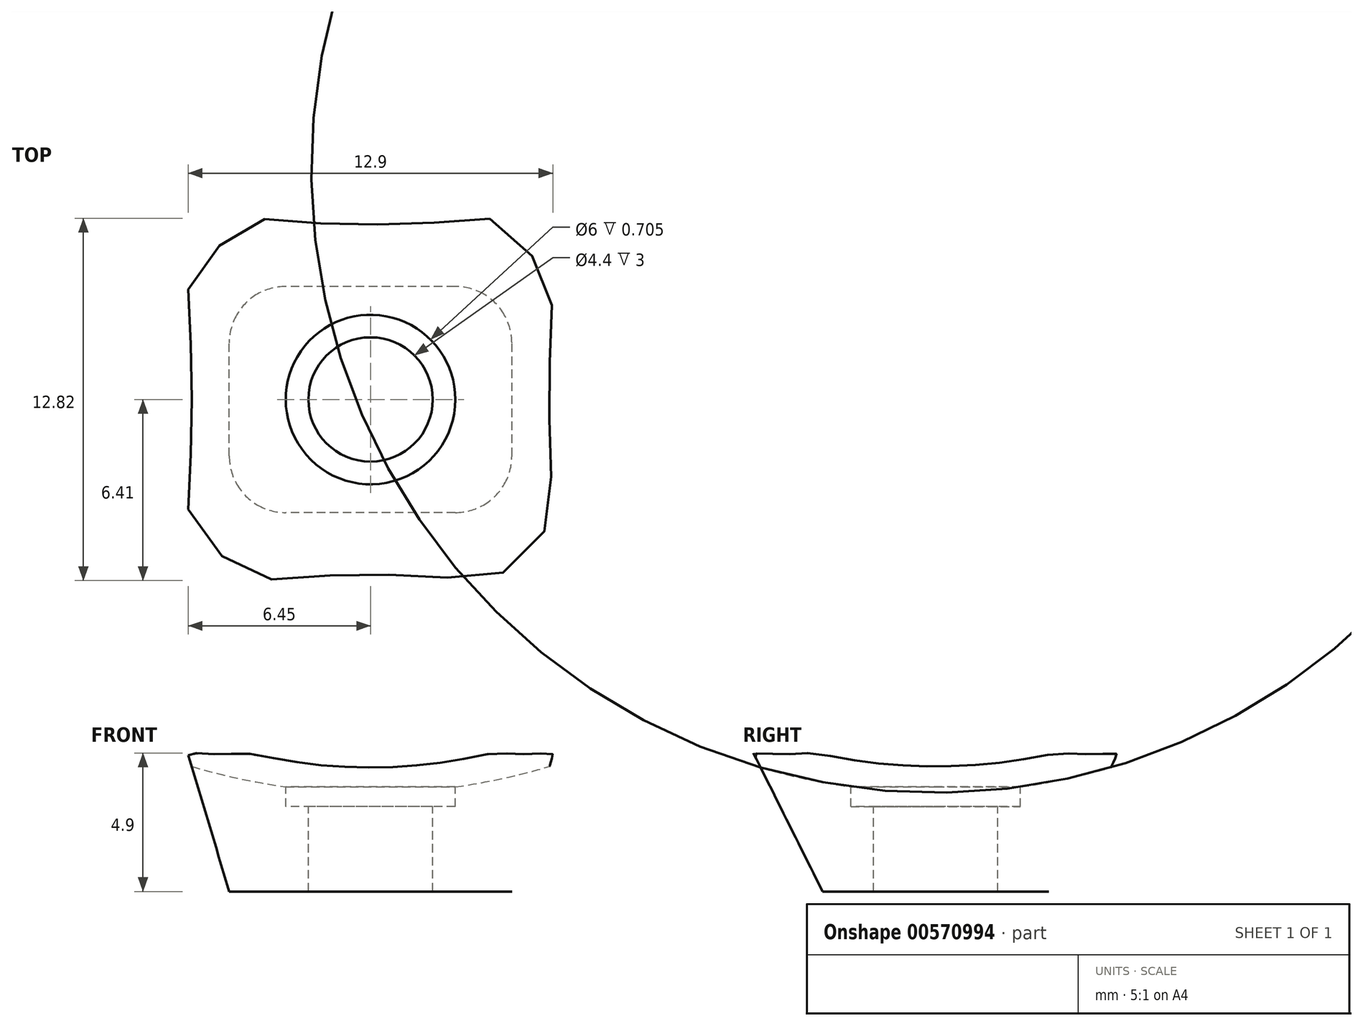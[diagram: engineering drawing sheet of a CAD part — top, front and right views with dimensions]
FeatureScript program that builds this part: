
annotation { "Feature Type Name" : "Feature", "Feature Type Description" : "" }
export const myFeature = defineFeature(function(context is Context, id is Id, definition is map)
    precondition{}
    {
        {
            var Q0;
            Q0=qCreatedBy(makeId("Top.planeOp"),FACE);
            var sketch = newSketch(context, id + "F0", { "sketchPlane" : qUnion([Q0])});
            skLineSegment(sketch, "E0.bottom", {"start": v(3, -4) * mm, "end": v(-3, -4) * mm});
            skLineSegment(sketch, "E0.top", {"start": v(3, 4) * mm, "end": v(-3, 4) * mm});
            skLineSegment(sketch, "E0.left", {"start": v(5, -2) * mm, "end": v(5, 2) * mm});
            skLineSegment(sketch, "E0.right", {"start": v(-5, -2) * mm, "end": v(-5, 2) * mm});
            skPoint(sketch, "E0.middle", {"position": v(0, 0) * mm});
            skPoint(sketch, "E1.visualSharp", {"position": v(-5, 4) * mm});
            skArc(sketch, "E1.filletArc", {"start": v(-3, 4) * mm, "mid": v(-4.41, 3.41) * mm, "end": v(-5, 2) * mm});
            skPoint(sketch, "E2.visualSharp", {"position": v(-5, -4) * mm});
            skArc(sketch, "E2.filletArc", {"start": v(-5, -2) * mm, "mid": v(-4.41, -3.41) * mm, "end": v(-3, -4) * mm});
            skPoint(sketch, "E3.visualSharp", {"position": v(5, -4) * mm});
            skArc(sketch, "E3.filletArc", {"start": v(3, -4) * mm, "mid": v(4.41, -3.41) * mm, "end": v(5, -2) * mm});
            skPoint(sketch, "E4.visualSharp", {"position": v(5, 4) * mm});
            skArc(sketch, "E4.filletArc", {"start": v(5, 2) * mm, "mid": v(4.41, 3.41) * mm, "end": v(3, 4) * mm});
            skSolve(sketch);
        }
        {
            var Q0;
            Q0=qCreatedBy(makeId("Right.planeOp"),FACE);
            var sketch = newSketch(context, id + "F1", { "sketchPlane" : qUnion([Q0])});
            skLineSegment(sketch, "E5", {"start": v(0, 0) * mm, "end": v(0, 5) * mm});
            skLineSegment(sketch, "E6", {"start": v(0, 5) * mm, "end": v(-8, 5) * mm, "construction": true});
            skPoint(sketch, "E7", {"position": v(0, 3.5) * mm});
            skLineSegment(sketch, "E8", {"start": v(0, 3.5) * mm, "end": v(-8, 3.5) * mm, "construction": true});
            skArc(sketch, "E9", {"start": v(-8, 5) * mm, "mid": v(-4.07, 3.88) * mm, "end": v(0, 3.5) * mm});
            skLineSegment(sketch, "E10", {"start": v(0, 5) * mm, "end": v(0, 7.01) * mm});
            skLineSegment(sketch, "E11", {"start": v(0, 7.01) * mm, "end": v(-8, 7.01) * mm});
            skLineSegment(sketch, "E12", {"start": v(-8, 7.01) * mm, "end": v(-8, 5) * mm});
            skLineSegment(sketch, "E13", {"start": v(0, 0) * mm, "end": v(-2.2, 0) * mm});
            skLineSegment(sketch, "E14", {"start": v(-3, 3) * mm, "end": v(-3, 3.7) * mm});
            skLineSegment(sketch, "E15", {"start": v(-2.2, 0) * mm, "end": v(-2.2, 3) * mm});
            skLineSegment(sketch, "E16", {"start": v(-2.2, 3) * mm, "end": v(-3, 3) * mm});
            skSolve(sketch);
        }
        {
            var Q0;
            Q0=qCreatedBy(makeId("Top.planeOp"),FACE);
            var Q1;
            Q1=sQuery(id+"F1.wireOp",VERTEX,"E5.end");
            cPlane(context, id + "F2", {"entities" : qUnion([Q0, Q1]), "cplaneType" : CPlaneType.PLANE_POINT, "offset" : 25 * mm, "width" : 150 * mm, "height" : 150 * mm});
        }
        {
            var Q0;
            Q0=qCreatedBy(id+"F2.planeOp",FACE);
            var sketch = newSketch(context, id + "F3", { "sketchPlane" : qUnion([Q0])});
            skLineSegment(sketch, "E17", {"start": v(-6.5, 3.96) * mm, "end": v(-6.5, -3.96) * mm});
            skLineSegment(sketch, "E18", {"start": v(6.5, 3.96) * mm, "end": v(6.5, -3.96) * mm});
            skLineSegment(sketch, "E19", {"start": v(-3.96, 6.5) * mm, "end": v(3.96, 6.5) * mm});
            skLineSegment(sketch, "E20", {"start": v(-3.96, -6.5) * mm, "end": v(3.96, -6.5) * mm});
            skLineSegment(sketch, "E21", {"start": v(-4.67, 6.2) * mm, "end": v(-6.2, 4.67) * mm});
            skLineSegment(sketch, "E22", {"start": v(4.67, 6.2) * mm, "end": v(6.2, 4.67) * mm});
            skLineSegment(sketch, "E23", {"start": v(6.2, -4.67) * mm, "end": v(4.67, -6.2) * mm});
            skLineSegment(sketch, "E24", {"start": v(-6.2, -4.67) * mm, "end": v(-4.67, -6.2) * mm});
            skPoint(sketch, "E25.visualSharp", {"position": v(-4.38, 6.5) * mm});
            skArc(sketch, "E25.filletArc", {"start": v(-3.96, 6.5) * mm, "mid": v(-4.35, 6.42) * mm, "end": v(-4.67, 6.2) * mm});
            skPoint(sketch, "E26.visualSharp", {"position": v(-6.5, 4.38) * mm});
            skArc(sketch, "E26.filletArc", {"start": v(-6.2, 4.67) * mm, "mid": v(-6.42, 4.35) * mm, "end": v(-6.5, 3.96) * mm});
            skPoint(sketch, "E27.visualSharp", {"position": v(-6.5, -4.38) * mm});
            skArc(sketch, "E27.filletArc", {"start": v(-6.5, -3.96) * mm, "mid": v(-6.42, -4.35) * mm, "end": v(-6.2, -4.67) * mm});
            skPoint(sketch, "E28.visualSharp", {"position": v(-4.38, -6.5) * mm});
            skArc(sketch, "E28.filletArc", {"start": v(-4.67, -6.2) * mm, "mid": v(-4.35, -6.42) * mm, "end": v(-3.96, -6.5) * mm});
            skPoint(sketch, "E29.visualSharp", {"position": v(4.38, -6.5) * mm});
            skArc(sketch, "E29.filletArc", {"start": v(3.96, -6.5) * mm, "mid": v(4.35, -6.42) * mm, "end": v(4.67, -6.2) * mm});
            skPoint(sketch, "E30.visualSharp", {"position": v(6.5, -4.38) * mm});
            skArc(sketch, "E30.filletArc", {"start": v(6.2, -4.67) * mm, "mid": v(6.42, -4.35) * mm, "end": v(6.5, -3.96) * mm});
            skPoint(sketch, "E31.visualSharp", {"position": v(6.5, 4.38) * mm});
            skArc(sketch, "E31.filletArc", {"start": v(6.5, 3.96) * mm, "mid": v(6.42, 4.35) * mm, "end": v(6.2, 4.67) * mm});
            skPoint(sketch, "E32.visualSharp", {"position": v(4.38, 6.5) * mm});
            skArc(sketch, "E32.filletArc", {"start": v(4.67, 6.2) * mm, "mid": v(4.35, 6.42) * mm, "end": v(3.96, 6.5) * mm});
            skSolve(sketch);
        }
        {
            var Q0;
            Q0=sQuery(id+"F3.wireOp",VERTEX,"E30.filletArc.end");
            var Q1;
            Q1=sQuery(id+"F0.wireOp",VERTEX,"E0.left.start");
            var Q2;
            Q2=sQuery(id+"F0.wireOp",VERTEX,"E0.middle");
            cPlane(context, id + "F4", {"entities" : qUnion([Q0, Q1, Q2]), "cplaneType" : CPlaneType.THREE_POINT, "offset" : 25 * mm, "width" : 150 * mm, "height" : 150 * mm});
        }
        {
            var Q0;
            Q0=sQuery(id+"F0.wireOp",VERTEX,"E0.middle");
            var Q1;
            Q1=sQuery(id+"F3.wireOp",VERTEX,"E31.filletArc.start");
            var Q2;
            Q2=sQuery(id+"F0.wireOp",VERTEX,"E0.left.end");
            cPlane(context, id + "F5", {"entities" : qUnion([Q0, Q1, Q2]), "cplaneType" : CPlaneType.THREE_POINT, "offset" : 25 * mm, "width" : 150 * mm, "height" : 150 * mm});
        }
        {
            var Q0;
            Q0=sQuery(id+"F3.wireOp",VERTEX,"E32.filletArc.end");
            var Q1;
            Q1=sQuery(id+"F0.wireOp",VERTEX,"E0.top.start");
            var Q2;
            Q2=sQuery(id+"F0.wireOp",VERTEX,"E0.middle");
            cPlane(context, id + "F6", {"entities" : qUnion([Q0, Q1, Q2]), "cplaneType" : CPlaneType.THREE_POINT, "offset" : 25 * mm, "width" : 150 * mm, "height" : 150 * mm});
        }
        {
            var Q0;
            Q0=sQuery(id+"F0.wireOp",VERTEX,"E0.middle");
            var Q1;
            Q1=sQuery(id+"F3.wireOp",VERTEX,"E25.filletArc.start");
            var Q2;
            Q2=sQuery(id+"F0.wireOp",VERTEX,"E1.filletArc.start");
            cPlane(context, id + "F7", {"entities" : qUnion([Q0, Q1, Q2]), "cplaneType" : CPlaneType.THREE_POINT, "offset" : 25 * mm, "width" : 150 * mm, "height" : 150 * mm});
        }
        {
            var Q0;
            Q0=sQuery(id+"F3.wireOp",VERTEX,"E17.start");
            var Q1;
            Q1=sQuery(id+"F0.wireOp",VERTEX,"E1.filletArc.end");
            var Q2;
            Q2=sQuery(id+"F0.wireOp",VERTEX,"E0.middle");
            cPlane(context, id + "F8", {"entities" : qUnion([Q0, Q1, Q2]), "cplaneType" : CPlaneType.THREE_POINT, "offset" : 25 * mm, "width" : 150 * mm, "height" : 150 * mm});
        }
        {
            var Q0;
            Q0=sQuery(id+"F3.wireOp",VERTEX,"E27.filletArc.start");
            var Q1;
            Q1=sQuery(id+"F0.wireOp",VERTEX,"E2.filletArc.start");
            var Q2;
            Q2=sQuery(id+"F0.wireOp",VERTEX,"E0.middle");
            cPlane(context, id + "F9", {"entities" : qUnion([Q0, Q1, Q2]), "cplaneType" : CPlaneType.THREE_POINT, "offset" : 25 * mm, "width" : 150 * mm, "height" : 150 * mm});
        }
        {
            var Q0;
            Q0=sQuery(id+"F3.wireOp",VERTEX,"E28.filletArc.end");
            var Q1;
            Q1=sQuery(id+"F0.wireOp",VERTEX,"E0.bottom.end");
            var Q2;
            Q2=sQuery(id+"F0.wireOp",VERTEX,"E0.middle");
            cPlane(context, id + "F10", {"entities" : qUnion([Q0, Q1, Q2]), "cplaneType" : CPlaneType.THREE_POINT, "offset" : 25 * mm, "width" : 150 * mm, "height" : 150 * mm});
        }
        {
            var Q0;
            Q0=sQuery(id+"F3.wireOp",VERTEX,"E29.filletArc.start");
            var Q1;
            Q1=sQuery(id+"F0.wireOp",VERTEX,"E0.bottom.start");
            var Q2;
            Q2=sQuery(id+"F1.wireOp",VERTEX,"E5.start");
            cPlane(context, id + "F11", {"entities" : qUnion([Q0, Q1, Q2]), "cplaneType" : CPlaneType.THREE_POINT, "offset" : 25 * mm, "width" : 150 * mm, "height" : 150 * mm});
        }
        {
            var Q0;
            Q0=qCreatedBy(id+"F4.planeOp",FACE);
            var sketch = newSketch(context, id + "F12", { "sketchPlane" : qUnion([Q0])});
            skLineSegment(sketch, "E33", {"start": v(6.97, 5.87) * mm, "end": v(5.36, 0.53) * mm});
            skSolve(sketch);
        }
        {
            var Q0;
            Q0=qCreatedBy(id+"F5.planeOp",FACE);
            var sketch = newSketch(context, id + "F13", { "sketchPlane" : qUnion([Q0])});
            skLineSegment(sketch, "E34", {"start": v(6.97, 5.87) * mm, "end": v(5.36, 0.53) * mm});
            skSolve(sketch);
        }
        {
            var Q0;
            Q0=qCreatedBy(id+"F6.planeOp",FACE);
            var sketch = newSketch(context, id + "F14", { "sketchPlane" : qUnion([Q0])});
            skLineSegment(sketch, "E35", {"start": v(8.08, 4.2) * mm, "end": v(4.97, -0.54) * mm});
            skSolve(sketch);
        }
        {
            var Q0;
            Q0=qCreatedBy(id+"F7.planeOp",FACE);
            var sketch = newSketch(context, id + "F15", { "sketchPlane" : qUnion([Q0])});
            skLineSegment(sketch, "E36", {"start": v(8.08, 4.2) * mm, "end": v(4.97, -0.54) * mm});
            skSolve(sketch);
        }
        {
            var Q0;
            Q0=qCreatedBy(id+"F8.planeOp",FACE);
            var sketch = newSketch(context, id + "F16", { "sketchPlane" : qUnion([Q0])});
            skLineSegment(sketch, "E37", {"start": v(6.97, 5.87) * mm, "end": v(5.36, 0.53) * mm});
            skSolve(sketch);
        }
        {
            var Q0;
            Q0=qCreatedBy(id+"F9.planeOp",FACE);
            var sketch = newSketch(context, id + "F17", { "sketchPlane" : qUnion([Q0])});
            skLineSegment(sketch, "E38", {"start": v(6.97, 5.87) * mm, "end": v(5.36, 0.53) * mm});
            skSolve(sketch);
        }
        {
            var Q0;
            Q0=qCreatedBy(id+"F10.planeOp",FACE);
            var sketch = newSketch(context, id + "F18", { "sketchPlane" : qUnion([Q0])});
            skLineSegment(sketch, "E39", {"start": v(8.08, 4.2) * mm, "end": v(4.97, -0.54) * mm});
            skSolve(sketch);
        }
        {
            var Q0;
            Q0=qCreatedBy(id+"F11.planeOp",FACE);
            var sketch = newSketch(context, id + "F19", { "sketchPlane" : qUnion([Q0])});
            skLineSegment(sketch, "E40", {"start": v(8.08, 4.2) * mm, "end": v(4.97, -0.54) * mm});
            skSolve(sketch);
        }
        {
            var Q0;
            Q0=makeQuery(id+"F3.imprint","IMPRINT",FACE,{"disambiguationData":[TD([[makeQuery(id+"F3.imprint","IMPRINT",EDGE,{"derivedFrom":sQuery(id+"F3.wireOp",EDGE,"E17")}),1.0]])]});
            var Q1;
            Q1=makeQuery(id+"F0.imprint","IMPRINT",FACE,{"disambiguationData":[TD([[makeQuery(id+"F0.imprint","IMPRINT",EDGE,{"derivedFrom":sQuery(id+"F0.wireOp",EDGE,"E0.bottom")}),-1.0]])]});
            var Q2;
            Q2=sQuery(id+"F18.wireOp",EDGE,"E39");
            var Q3;
            Q3=sQuery(id+"F19.wireOp",EDGE,"E40");
            var Q4;
            Q4=sQuery(id+"F12.wireOp",EDGE,"E33");
            var Q5;
            Q5=sQuery(id+"F13.wireOp",EDGE,"E34");
            var Q6;
            Q6=sQuery(id+"F14.wireOp",EDGE,"E35");
            var Q7;
            Q7=sQuery(id+"F15.wireOp",EDGE,"E36");
            var Q8;
            Q8=sQuery(id+"F16.wireOp",EDGE,"E37");
            var Q9;
            Q9=sQuery(id+"F17.wireOp",EDGE,"E38");
            loft(context, id + "F20", {"addGuides" : true, "sheetProfilesArray" : [{ "sheetProfileEntities" : qUnion([Q0]) }, { "sheetProfileEntities" : qUnion([Q1]) }], "guidesArray" : [{ "guideEntities" : qUnion([Q2]), "guideDerivativeType" : LoftGuideDerivativeType.DEFAULT, "guideDerivativeMagnitude" : 1 }, { "guideEntities" : qUnion([Q3]), "guideDerivativeType" : LoftGuideDerivativeType.DEFAULT, "guideDerivativeMagnitude" : 1 }, { "guideEntities" : qUnion([Q4]), "guideDerivativeType" : LoftGuideDerivativeType.DEFAULT, "guideDerivativeMagnitude" : 1 }, { "guideEntities" : qUnion([Q5]), "guideDerivativeType" : LoftGuideDerivativeType.DEFAULT, "guideDerivativeMagnitude" : 1 }, { "guideEntities" : qUnion([Q6]), "guideDerivativeType" : LoftGuideDerivativeType.DEFAULT, "guideDerivativeMagnitude" : 1 }, { "guideEntities" : qUnion([Q7]), "guideDerivativeType" : LoftGuideDerivativeType.DEFAULT, "guideDerivativeMagnitude" : 1 }, { "guideEntities" : qUnion([Q8]), "guideDerivativeType" : LoftGuideDerivativeType.DEFAULT, "guideDerivativeMagnitude" : 1 }, { "guideEntities" : qUnion([Q9]), "guideDerivativeType" : LoftGuideDerivativeType.DEFAULT, "guideDerivativeMagnitude" : 1 }]});
        }
        {
            var Q0;
            {var subQ0=sQuery(id+"F1.wireOp",EDGE,"E10");Q0=makeQuery(id+"F1.imprint","IMPRINT",FACE,{"disambiguationData":[TD([[makeQuery(id+"F1.imprint","IMPRINT",EDGE,{"derivedFrom":subQ0}),1.0]])]});}
            var Q1;
            {var subQ0=sQuery(id+"F1.wireOp",EDGE,"E13");Q1=makeQuery(id+"F1.imprint","IMPRINT",FACE,{"disambiguationData":[TD([[makeQuery(id+"F1.imprint","IMPRINT",EDGE,{"derivedFrom":subQ0}),-1.0]])]});}
            var Q2;
            Q2=sQuery(id+"F1.wireOp",EDGE,"E5");
            revolve(context, id + "F21", {"operationType" : NewBodyOperationType.REMOVE, "entities" : qUnion([Q0, Q1]), "axis" : qUnion([Q2]), "revolveType" : RevolveType.FULL, "oppositeDirection" : true});
        }
    });
